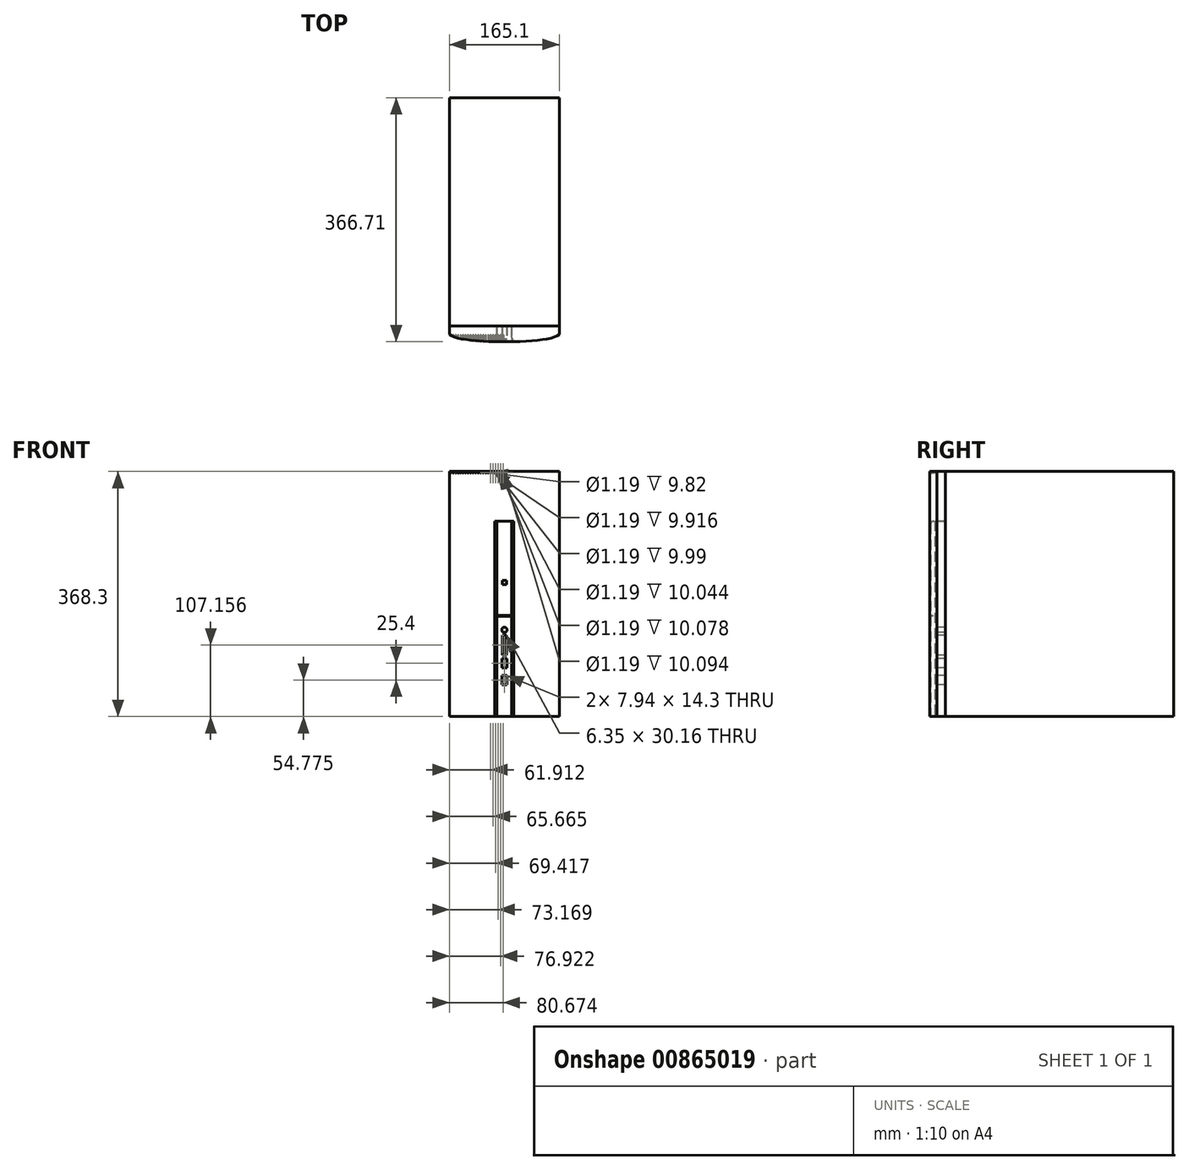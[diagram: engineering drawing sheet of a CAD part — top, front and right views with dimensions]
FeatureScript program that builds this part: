
annotation { "Feature Type Name" : "Feature", "Feature Type Description" : "" }
export const myFeature = defineFeature(function(context is Context, id is Id, definition is map)
    precondition{}
    {
        {
            var Q0;
            Q0=qCreatedBy(makeId("Top.planeOp"),FACE);
            var sketch = newSketch(context, id + "F0", { "sketchPlane" : qUnion([Q0])});
            skLineSegment(sketch, "E0.bottom", {"start": v(82.55, 171.45) * mm, "end": v(-82.55, 171.45) * mm});
            skLineSegment(sketch, "E0.top", {"start": v(82.55, -171.45) * mm, "end": v(-82.55, -171.45) * mm});
            skLineSegment(sketch, "E0.left", {"start": v(82.55, 171.45) * mm, "end": v(82.55, -171.45) * mm});
            skLineSegment(sketch, "E0.right", {"start": v(-82.55, 171.45) * mm, "end": v(-82.55, -171.45) * mm});
            skPoint(sketch, "E0.middle", {"position": v(0, 0) * mm});
            skSolve(sketch);
        }
        {
            var Q0;
            Q0 = qSketchRegion(id + "F0", true);
            extrude(context, id + "F1", {"entities" : qUnion([Q0]), "depth" : 368.3 * mm, "offsetDistance" : 25.4 * mm});
        }
        {
            var Q0;
            Q0=qCreatedBy(makeId("Top.planeOp"),FACE);
            var sketch = newSketch(context, id + "F2", { "sketchPlane" : qUnion([Q0])});
            skLineSegment(sketch, "E1.bottom", {"start": v(-82.55, -171.45) * mm, "end": v(82.55, -171.45) * mm});
            skLineSegment(sketch, "E1.top", {"start": v(-82.55, -184.15) * mm, "end": v(82.55, -184.15) * mm});
            skLineSegment(sketch, "E1.left", {"start": v(-82.55, -171.45) * mm, "end": v(-82.55, -184.15) * mm});
            skLineSegment(sketch, "E1.right", {"start": v(82.55, -171.45) * mm, "end": v(82.55, -184.15) * mm});
            skFitSpline(sketch, "E2", {"points": [v(-82.55, -184.15) * mm, v(0, -195.26) * mm, v(82.55, -184.15) * mm], "startDerivative": vector(58, -53.1) * mm, "endDerivative": vector(58, 53.1) * mm});
            skSolve(sketch);
        }
        {
            var Q0;
            Q0 = qSketchRegion(id + "F2", true);
            var Q1;
            Q1=makeQuery(id+"F1.opExtrude","CAP_FACE",FACE,{"disambiguationData":[OSD([sQuery(id+"F0.wireOp",EDGE,"E0.bottom"),sQuery(id+"F0.wireOp",EDGE,"E0.top"),sQuery(id+"F0.wireOp",EDGE,"E0.left"),sQuery(id+"F0.wireOp",EDGE,"E0.right")])],"isStart":false});
            extrude(context, id + "F3", {"entities" : qUnion([Q0]), "endBound" : BoundingType.UP_TO_SURFACE, "depth" : 368.3 * mm, "endBoundEntityFace" : qUnion([Q1]), "offsetDistance" : 25.4 * mm});
        }
        {
            var Q0;
            Q0=makeQuery(id+"F3.opExtrude","CAP_FACE",FACE,{"disambiguationData":[OSD([sQuery(id+"F2.wireOp",EDGE,"E1.bottom"),sQuery(id+"F2.wireOp",EDGE,"E1.left"),sQuery(id+"F2.wireOp",EDGE,"E1.right"),sQuery(id+"F2.wireOp",EDGE,"E2")])],"isStart":true});
            var sketch = newSketch(context, id + "F4", { "sketchPlane" : qUnion([Q0])});
            skLineSegment(sketch, "E3", {"start": v(-14.29, 195.14) * mm, "end": v(14.29, 195.14) * mm, "construction": true});
            skLineSegment(sketch, "E4.bottom", {"start": v(-11.11, 171.45) * mm, "end": v(11.11, 171.45) * mm});
            skLineSegment(sketch, "E4.top", {"start": v(-11.11, 187.33) * mm, "end": v(11.11, 187.33) * mm});
            skLineSegment(sketch, "E4.left", {"start": v(-11.11, 171.45) * mm, "end": v(-11.11, 187.33) * mm});
            skLineSegment(sketch, "E4.right", {"start": v(11.11, 171.45) * mm, "end": v(11.11, 187.33) * mm});
            skLineSegment(sketch, "E5", {"start": v(-11.11, 187.33) * mm, "end": v(-14.34, 195.26) * mm});
            skLineSegment(sketch, "E6", {"start": v(-14.34, 195.26) * mm, "end": v(14.34, 195.26) * mm});
            skLineSegment(sketch, "E7", {"start": v(14.34, 195.26) * mm, "end": v(11.11, 187.33) * mm});
            skSolve(sketch);
        }
        {
            var Q0;
            Q0 = qSketchRegion(id + "F4", true);
            extrude(context, id + "F5", {"entities" : qUnion([Q0]), "operationType" : NewBodyOperationType.REMOVE, "oppositeDirection" : true, "depth" : 293.7 * mm, "offsetDistance" : 25.4 * mm});
        }
        {
            var Q0;
            {var subQ0=sQuery(id+"F2.wireOp",EDGE,"E2");var subQ1=sQuery(id+"F2.wireOp",EDGE,"E1.right");var subQ2=sQuery(id+"F2.wireOp",EDGE,"E1.bottom");Q0=makeQuery(id+"F5.boolean.opBoolean","SPLIT",FACE,{"disambiguationData":[TD([makeQuery(id+"F3.opExtrude","SWEPT_FACE",FACE,{"disambiguationData":[OSD([subQ1])]})])],"derivedFrom":makeQuery(id+"F3.opExtrude","CAP_FACE",FACE,{"disambiguationData":[OSD([subQ2,sQuery(id+"F2.wireOp",EDGE,"E1.left"),subQ1,subQ0])],"isStart":true})});}
            var sketch = newSketch(context, id + "F6", { "sketchPlane" : qUnion([Q0])});
            skLineSegment(sketch, "E8.bottom", {"start": v(-11.11, 171.45) * mm, "end": v(11.11, 171.45) * mm});
            skLineSegment(sketch, "E8.top", {"start": v(-11.11, 193.68) * mm, "end": v(11.11, 193.68) * mm});
            skLineSegment(sketch, "E8.left", {"start": v(-11.11, 171.45) * mm, "end": v(-11.11, 193.68) * mm});
            skLineSegment(sketch, "E8.right", {"start": v(11.11, 171.45) * mm, "end": v(11.11, 193.68) * mm});
            skPoint(sketch, "E9.visualSharp", {"position": v(-11.11, 193.68) * mm});
            skPoint(sketch, "E10.visualSharp", {"position": v(11.11, 193.68) * mm});
            skSolve(sketch);
        }
        {
            var Q0;
            {var subQ1=sQuery(id+"F6.wireOp",EDGE,"E8.bottom");Q0=makeQuery(id+"F6.imprint","IMPRINT",FACE,{"disambiguationData":[TD([[makeQuery(id+"F6.imprint","IMPRINT",EDGE,{"derivedFrom":subQ1}),1.0]])]});}
            var Q1;
            Q1=makeQuery(id+"F5.boolean.opBoolean","COPY",FACE,{"derivedFrom":makeQuery(id+"F5.opExtrude","CAP_FACE",FACE,{"disambiguationData":[OSD([sQuery(id+"F4.wireOp",EDGE,"E4.bottom"),sQuery(id+"F4.wireOp",EDGE,"E4.left"),sQuery(id+"F4.wireOp",EDGE,"E4.right"),sQuery(id+"F4.wireOp",EDGE,"E5"),sQuery(id+"F4.wireOp",EDGE,"E6"),sQuery(id+"F4.wireOp",EDGE,"E7")])],"isStart":false})});
            extrude(context, id + "F7", {"entities" : qUnion([Q0]), "endBound" : BoundingType.UP_TO_SURFACE, "oppositeDirection" : true, "depth" : 53.85 * mm, "endBoundEntityFace" : qUnion([Q1]), "offsetDistance" : 25.4 * mm});
        }
        {
            var Q0;
            Q0=makeQuery(id+"F7.opExtrude","CAP_EDGE",EDGE,{"disambiguationData":[OSD([sQuery(id+"F6.wireOp",EDGE,"E8.top")])],"isStart":false});
            fillet(context, id + "F8", {"entities" : qUnion([Q0]), "radius" : 5.08 * mm, "tangentPropagation" : true, "allowEdgeOverflow" : false});
        }
        {
            var Q0;
            Q0=makeQuery(id+"F7.opExtrude","SWEPT_FACE",FACE,{"disambiguationData":[OSD([sQuery(id+"F6.wireOp",EDGE,"E8.top")])]});
            var sketch = newSketch(context, id + "F9", { "sketchPlane" : qUnion([Q0])});
            skLineSegment(sketch, "E11.bottom", {"start": v(-11.11, 152) * mm, "end": v(11.11, 152) * mm});
            skLineSegment(sketch, "E11.top", {"start": v(-11.11, 150.81) * mm, "end": v(11.11, 150.81) * mm});
            skLineSegment(sketch, "E11.left", {"start": v(-11.11, 152) * mm, "end": v(-11.11, 150.81) * mm});
            skLineSegment(sketch, "E11.right", {"start": v(11.11, 152) * mm, "end": v(11.11, 150.81) * mm});
            skSolve(sketch);
        }
        {
            var Q0;
            Q0 = qSketchRegion(id + "F9", true);
            extrude(context, id + "F10", {"entities" : qUnion([Q0]), "operationType" : NewBodyOperationType.REMOVE, "oppositeDirection" : true, "depth" : 3.17 * mm, "offsetDistance" : 25.4 * mm});
        }
        {
            var Q0;
            {var subQ0=sQuery(id+"F6.wireOp",EDGE,"E8.top");Q0=makeQuery(id+"F10.boolean.opBoolean","SPLIT",FACE,{"disambiguationData":[TD([makeQuery(id+"F8.opFillet","BLEND_FACE",FACE,{"disambiguationData":[OSD([subQ0])]})])],"derivedFrom":makeQuery(id+"F7.opExtrude","SWEPT_FACE",FACE,{"disambiguationData":[OSD([subQ0])]})});}
            var sketch = newSketch(context, id + "F11", { "sketchPlane" : qUnion([Q0])});
            skLineSegment(sketch, "E12.bottom", {"start": v(3.18, 198.04) * mm, "end": v(-3.17, 198.04) * mm});
            skLineSegment(sketch, "E12.top", {"start": v(3.18, 204.4) * mm, "end": v(-3.17, 204.4) * mm});
            skLineSegment(sketch, "E12.left", {"start": v(3.18, 198.04) * mm, "end": v(3.18, 204.4) * mm});
            skLineSegment(sketch, "E12.right", {"start": v(-3.17, 198.04) * mm, "end": v(-3.17, 204.4) * mm});
            skPoint(sketch, "E12.middle", {"position": v(0, 201.22) * mm});
            skPoint(sketch, "E12.middle.positionSnap0", {"position": v(0, 288.6) * mm});
            skPoint(sketch, "E12.centerSnap0", {"position": v(0, 288.6) * mm});
            skSolve(sketch);
        }
        {
            var Q0;
            Q0=makeQuery(id+"F11.imprint","IMPRINT",FACE,{"disambiguationData":[TD([[makeQuery(id+"F11.imprint","IMPRINT",EDGE,{"derivedFrom":sQuery(id+"F11.wireOp",EDGE,"E12.bottom")}),-1.0]])]});
            extrude(context, id + "F12", {"entities" : qUnion([Q0]), "operationType" : NewBodyOperationType.ADD, "depth" : 0.8 * mm, "offsetDistance" : 25.4 * mm});
        }
        {
            var Q0;
            {var subQ2=sQuery(id+"F6.wireOp",EDGE,"E8.top");Q0=makeQuery(id+"F10.boolean.opBoolean","SPLIT",FACE,{"disambiguationData":[TD([makeQuery(id+"F10.opExtrude","SWEPT_FACE",FACE,{"disambiguationData":[OSD([sQuery(id+"F9.wireOp",EDGE,"E11.top")])]})])],"derivedFrom":makeQuery(id+"F7.opExtrude","SWEPT_FACE",FACE,{"disambiguationData":[OSD([subQ2])]})});}
            var sketch = newSketch(context, id + "F13", { "sketchPlane" : qUnion([Q0])});
            skCircle(sketch, "E13", {"center": v(0, 130.18) * mm, "radius": 3.97 * mm});
            skLineSegment(sketch, "E14.bottom", {"start": v(3.17, 92.08) * mm, "end": v(-3.18, 92.08) * mm});
            skLineSegment(sketch, "E14.top", {"start": v(3.17, 122.24) * mm, "end": v(-3.18, 122.24) * mm});
            skLineSegment(sketch, "E14.left", {"start": v(3.17, 92.08) * mm, "end": v(3.17, 122.24) * mm});
            skLineSegment(sketch, "E14.right", {"start": v(-3.18, 92.08) * mm, "end": v(-3.18, 122.24) * mm});
            skPoint(sketch, "E14.middle", {"position": v(0, 107.16) * mm});
            skLineSegment(sketch, "E15.bottom", {"start": v(3.97, 73.03) * mm, "end": v(-3.97, 73.03) * mm});
            skLineSegment(sketch, "E15.top", {"start": v(3.97, 87.33) * mm, "end": v(-3.97, 87.33) * mm});
            skLineSegment(sketch, "E15.left", {"start": v(3.97, 73.03) * mm, "end": v(3.97, 87.33) * mm});
            skLineSegment(sketch, "E15.right", {"start": v(-3.97, 73.03) * mm, "end": v(-3.97, 87.33) * mm});
            skPoint(sketch, "E15.middle", {"position": v(0, 80.18) * mm});
            skLineSegment(sketch, "E16.bottom", {"start": v(3.97, 47.63) * mm, "end": v(-3.97, 47.63) * mm});
            skLineSegment(sketch, "E16.top", {"start": v(3.97, 61.93) * mm, "end": v(-3.97, 61.93) * mm});
            skLineSegment(sketch, "E16.left", {"start": v(3.97, 47.63) * mm, "end": v(3.97, 61.93) * mm});
            skLineSegment(sketch, "E16.right", {"start": v(-3.97, 47.62) * mm, "end": v(-3.97, 61.93) * mm});
            skPoint(sketch, "E16.middle", {"position": v(0, 54.78) * mm});
            skSolve(sketch);
        }
        {
            var Q0;
            Q0 = qSketchRegion(id + "F13", true);
            var Q1;
            Q1=makeQuery(id+"F1.opExtrude","SWEPT_BODY",BODY,{"disambiguationData":[OSD([sQuery(id+"F0.wireOp",EDGE,"E0.bottom"),sQuery(id+"F0.wireOp",EDGE,"E0.top"),sQuery(id+"F0.wireOp",EDGE,"E0.left"),sQuery(id+"F0.wireOp",EDGE,"E0.right")])]});
            extrude(context, id + "F14", {"entities" : qUnion([Q0]), "operationType" : NewBodyOperationType.REMOVE, "endBound" : BoundingType.UP_TO_BODY, "oppositeDirection" : true, "depth" : 25.4 * mm, "endBoundEntityBody" : qUnion([Q1]), "offsetDistance" : 25.4 * mm});
        }
        {
            var Q0;
            Q0=qCreatedBy(makeId("Front.planeOp"),FACE);
            cPlane(context, id + "F15", {"entities" : qUnion([Q0]), "cplaneType" : CPlaneType.OFFSET, "offset" : 195.33 * mm, "width" : 152.4 * mm, "height" : 152.4 * mm});
        }
        {
            var Q0;
            Q0=qCreatedBy(id+"F15.planeOp",FACE);
            var sketch = newSketch(context, id + "F16", { "sketchPlane" : qUnion([Q0])});
            skCircle(sketch, "E17", {"center": v(-1.88, 366.32) * mm, "radius": 0.6 * mm});
            skLineSegment(sketch, "E18", {"start": v(0, 368.3) * mm, "end": v(0, 0) * mm, "construction": true});
            skCircle(sketch, "E19.1.0.0", {"center": v(-5.63, 366.32) * mm, "radius": 0.6 * mm});
            skCircle(sketch, "E19.2.0.0", {"center": v(-9.38, 366.32) * mm, "radius": 0.6 * mm});
            skLineSegment(sketch, "E19.direction1", {"start": v(-1.88, 366.32) * mm, "end": v(-5.63, 366.32) * mm, "construction": true});
            skLineSegment(sketch, "E19.direction2", {"start": v(-1.88, 366.32) * mm, "end": v(-1.88, 362.56) * mm, "construction": true});
            skCircle(sketch, "E20.0.3.0", {"center": v(-13.13, 366.32) * mm, "radius": 0.6 * mm});
            skCircle(sketch, "E20.0.4.0", {"center": v(-16.89, 366.32) * mm, "radius": 0.6 * mm});
            skCircle(sketch, "E20.0.5.0", {"center": v(-20.64, 366.32) * mm, "radius": 0.6 * mm});
            skCircle(sketch, "E20.0.6.0", {"center": v(-24.39, 366.32) * mm, "radius": 0.6 * mm});
            skCircle(sketch, "E20.0.7.0", {"center": v(-28.14, 366.32) * mm, "radius": 0.6 * mm});
            skCircle(sketch, "E20.0.8.0", {"center": v(-31.9, 366.32) * mm, "radius": 0.6 * mm});
            skCircle(sketch, "E20.0.9.0", {"center": v(-35.65, 366.32) * mm, "radius": 0.6 * mm});
            skCircle(sketch, "E20.0.10.0", {"center": v(-39.4, 366.32) * mm, "radius": 0.6 * mm});
            skCircle(sketch, "E20.0.11.0", {"center": v(-43.15, 366.32) * mm, "radius": 0.6 * mm});
            skCircle(sketch, "E20.0.12.0", {"center": v(-46.9, 366.32) * mm, "radius": 0.6 * mm});
            skCircle(sketch, "E20.0.13.0", {"center": v(-50.66, 366.32) * mm, "radius": 0.6 * mm});
            skCircle(sketch, "E20.0.14.0", {"center": v(-54.4, 366.32) * mm, "radius": 0.6 * mm});
            skCircle(sketch, "E20.0.15.0", {"center": v(-58.16, 366.32) * mm, "radius": 0.6 * mm});
            skCircle(sketch, "E20.0.16.0", {"center": v(-61.91, 366.32) * mm, "radius": 0.6 * mm});
            skCircle(sketch, "E20.0.17.0", {"center": v(-65.66, 366.32) * mm, "radius": 0.6 * mm});
            skCircle(sketch, "E20.0.18.0", {"center": v(-69.42, 366.32) * mm, "radius": 0.6 * mm});
            skCircle(sketch, "E20.0.19.0", {"center": v(-73.17, 366.32) * mm, "radius": 0.6 * mm});
            skCircle(sketch, "E20.0.20.0", {"center": v(-76.92, 366.32) * mm, "radius": 0.6 * mm});
            skCircle(sketch, "E20.0.21.0", {"center": v(-80.67, 366.32) * mm, "radius": 0.6 * mm});
            skLineSegment(sketch, "E21", {"start": v(-1.88, 366.32) * mm, "end": v(-1.88, 368.3) * mm, "construction": true});
            skLineSegment(sketch, "E22", {"start": v(-1.88, 366.32) * mm, "end": v(0, 366.32) * mm, "construction": true});
            skLineSegment(sketch, "E23", {"start": v(-80.67, 366.32) * mm, "end": v(-82.55, 366.32) * mm, "construction": true});
            skLineSegment(sketch, "E24", {"start": v(-79.14, 1.98) * mm, "end": v(-79.14, 0) * mm, "construction": true});
            skPoint(sketch, "E25", {"position": v(-3.75, 368.3) * mm});
            skPoint(sketch, "E25.positionSnap0", {"position": v(-3.75, 366.32) * mm});
            skLineSegment(sketch, "E26", {"start": v(-3.75, 368.3) * mm, "end": v(-1.88, 368.3) * mm, "construction": true});
            skSolve(sketch);
        }
        {
            var Q0;
            Q0 = qSketchRegion(id + "F16", true);
            extrude(context, id + "F17", {"entities" : qUnion([Q0]), "operationType" : NewBodyOperationType.REMOVE, "oppositeDirection" : true, "depth" : 10.16 * mm, "offsetDistance" : 25.4 * mm});
        }
    });
